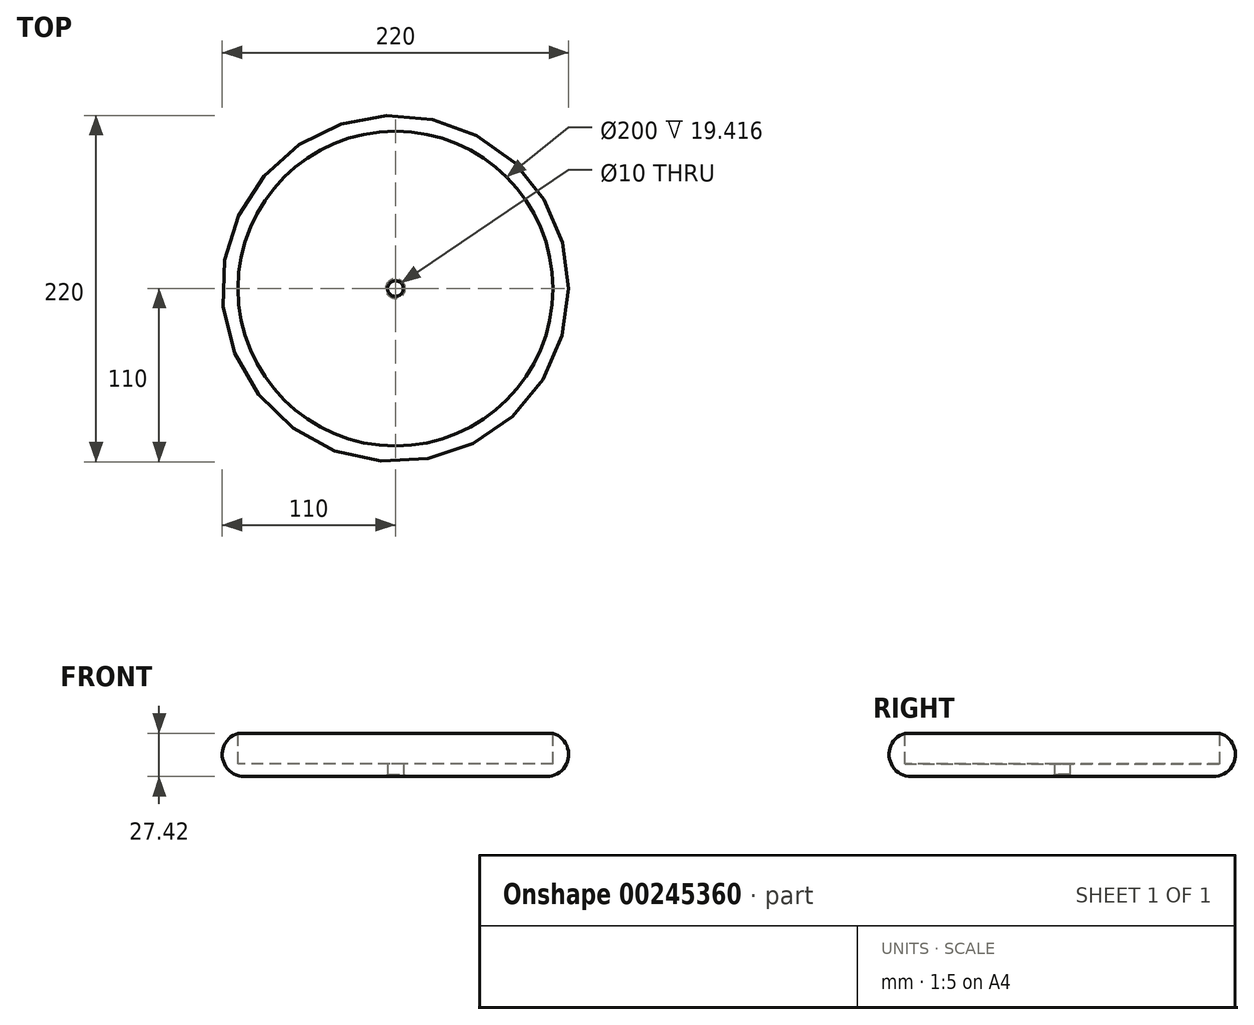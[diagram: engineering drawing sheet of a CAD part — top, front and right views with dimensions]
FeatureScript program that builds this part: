
annotation { "Feature Type Name" : "Feature", "Feature Type Description" : "" }
export const myFeature = defineFeature(function(context is Context, id is Id, definition is map)
    precondition{}
    {
        {
            var Q0;
            Q0=qCreatedBy(makeId("Top.planeOp"),FACE);
            var sketch = newSketch(context, id + "F0", { "sketchPlane" : qUnion([Q0])});
            skCircle(sketch, "E0", {"center": v(0, 0) * mm, "radius": 110 * mm});
            skSolve(sketch);
        }
        {
            var Q0;
            Q0=makeQuery(id+"F0.imprint","IMPRINT",FACE,{"disambiguationData":[TD([[makeQuery(id+"F0.imprint","IMPRINT",EDGE,{"derivedFrom":sQuery(id+"F0.wireOp",EDGE,"E0")}),1.0]])]});
            extrude(context, id + "F1", {"entities" : qUnion([Q0]), "depth" : 28 * mm, "offsetDistance" : 25 * mm});
        }
        {
            var Q0;
            Q0=makeQuery(id+"F1.opExtrude","CAP_EDGE",EDGE,{"disambiguationData":[OSD([sQuery(id+"F0.wireOp",EDGE,"E0")])],"isStart":false});
            var Q1;
            Q1=makeQuery(id+"F1.opExtrude","CAP_EDGE",EDGE,{"disambiguationData":[OSD([sQuery(id+"F0.wireOp",EDGE,"E0")])],"isStart":true});
            fillet(context, id + "F2", {"entities" : qUnion([Q0, Q1]), "radius" : 14 * mm, "tangentPropagation" : true, "allowEdgeOverflow" : false});
        }
        {
            var Q0;
            Q0=makeQuery(id+"F1.opExtrude","CAP_FACE",FACE,{"disambiguationData":[OSD([sQuery(id+"F0.wireOp",EDGE,"E0")])],"isStart":false});
            var sketch = newSketch(context, id + "F3", { "sketchPlane" : qUnion([Q0])});
            skCircle(sketch, "E1", {"center": v(0, 0) * mm, "radius": 100 * mm});
            skSolve(sketch);
        }
        {
            var Q0;
            Q0=qSketchRegion(id+"F3",true);
            extrude(context, id + "F4", {"entities" : qUnion([Q0]), "operationType" : NewBodyOperationType.REMOVE, "oppositeDirection" : true, "depth" : 20 * mm, "offsetDistance" : 25 * mm});
        }
        {
            var Q0;
            Q0=makeQuery(id+"F1.opExtrude","CAP_FACE",FACE,{"disambiguationData":[OSD([sQuery(id+"F0.wireOp",EDGE,"E0")])],"isStart":true});
            var sketch = newSketch(context, id + "F5", { "sketchPlane" : qUnion([Q0])});
            skPoint(sketch, "E2", {"position": v(0, 0) * mm});
            skSolve(sketch);
        }
        {
            var Q0;
            Q0=sQuery(id+"F5.wireOp",VERTEX,"E2");
            var Q1;
            Q1=makeQuery(id+"F1.opExtrude","SWEPT_BODY",BODY,{"disambiguationData":[OSD([sQuery(id+"F0.wireOp",EDGE,"E0")])]});
            hole(context, id + "F6", {"style" : HoleStyle.C_SINK, "endStyle" : HoleEndStyle.THROUGH, "holeDiameter" : 10 * mm, "cSinkDiameter" : 12.5 * mm, "cSinkAngle" : 90 * degree, "majorDiameter" : 5 * mm, "isTappedThrough" : true, "tappedDepth" : 12 * mm, "tapClearance" : 3, "locations" : qUnion([Q0]), "scope" : qUnion([Q1])});
        }
    });
